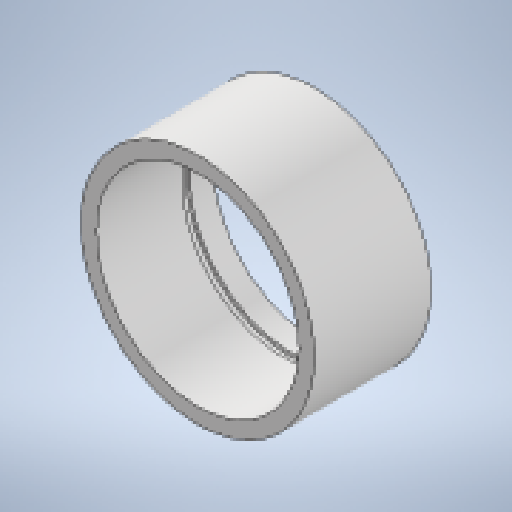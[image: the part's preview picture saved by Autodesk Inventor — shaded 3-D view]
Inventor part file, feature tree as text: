
AUTODESK INVENTOR PART (.ipt)
format: ipt  version: 2025.1 (Build 291241020, 241B)  size: 161,792 bytes
history: native  units: mm
features: revolve x1, sketch x1
ambient origin geometry x8: Origin, YZ Plane, XZ Plane, XY Plane, X Axis, Y Axis, Z Axis, Center Point
bodies: Solid1 (feature_tree)
feature tree (2):
  revolve  "Revolution1"  [1 undecoded]
  sketch  "Sketch1"  dims[d0=4.0mm d1=30.0mm d2=52.0mm d3=360.0deg d4=2.0mm d5=6.0mm d6=1.0mm]
note: 1 required parameter value undecoded (feature->parameter linkage not recoverable at this tier; creation-order binding heuristic only, values carry confidence <= 0.55)
